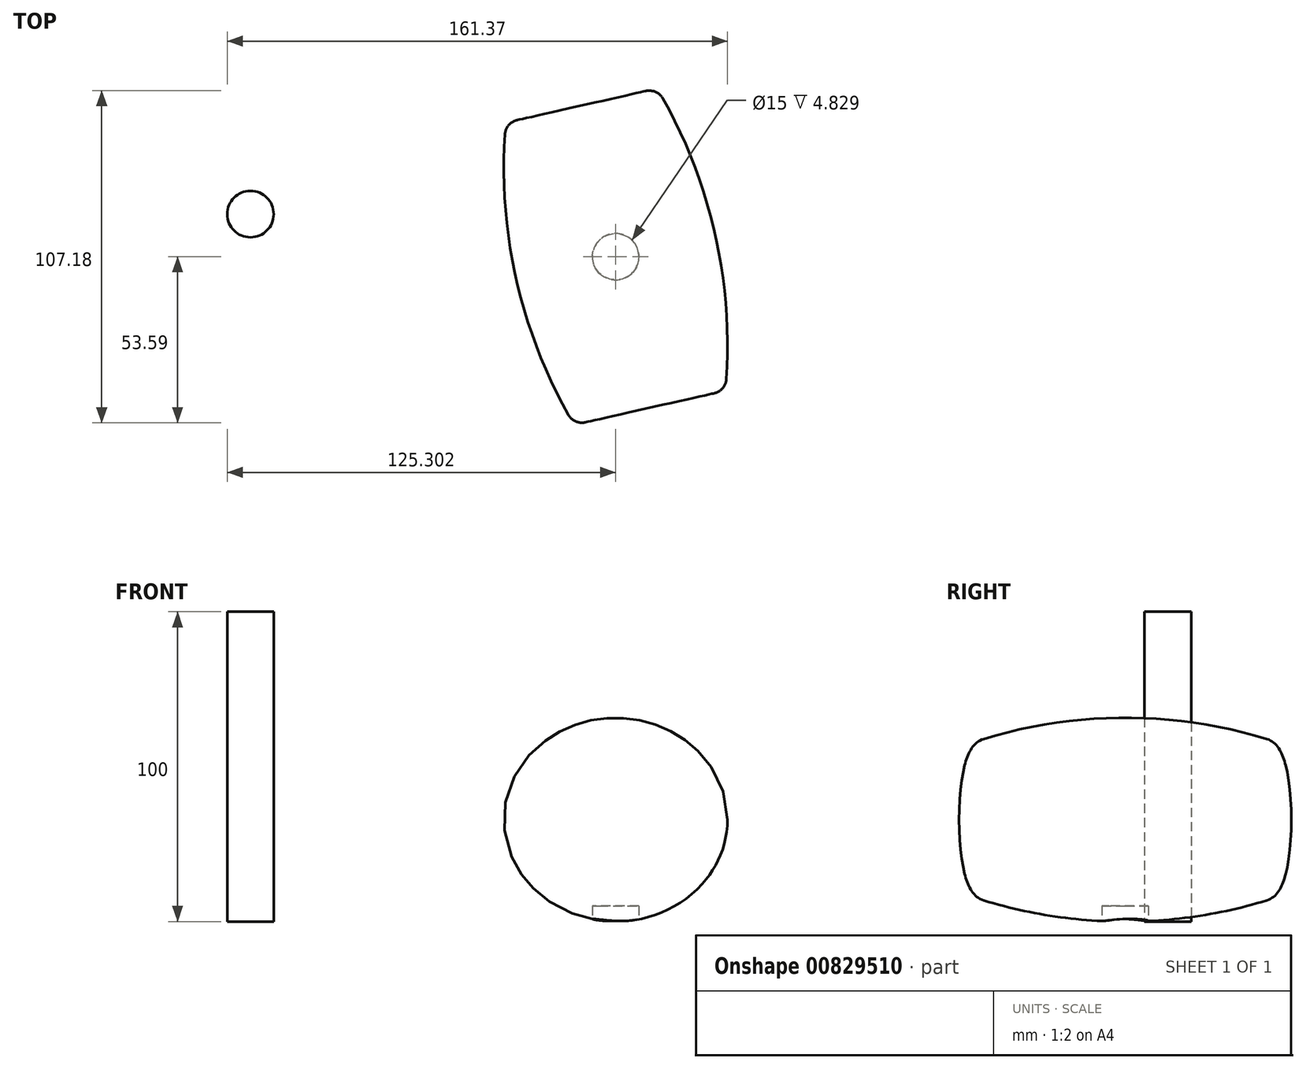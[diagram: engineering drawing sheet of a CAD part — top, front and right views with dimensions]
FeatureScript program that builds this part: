
annotation { "Feature Type Name" : "Feature", "Feature Type Description" : "" }
export const myFeature = defineFeature(function(context is Context, id is Id, definition is map)
    precondition{}
    {
        {
            var Q0;
            Q0=qCreatedBy(makeId("Top.planeOp"),FACE);
            var sketch = newSketch(context, id + "F0", { "sketchPlane" : qUnion([Q0])});
            skCircle(sketch, "E0", {"center": v(-56.5, 2) * mm, "radius": 7.5 * mm});
            skSolve(sketch);
        }
        {
            var Q0;
            Q0=makeQuery(id+"F0.imprint","IMPRINT",FACE,{"disambiguationData":[TD([[makeQuery(id+"F0.imprint","IMPRINT",EDGE,{"derivedFrom":sQuery(id+"F0.wireOp",EDGE,"E0")}),1.0]])]});
            extrude(context, id + "F1", {"entities" : qUnion([Q0]), "depth" : 100 * mm, "offsetDistance" : 25 * mm});
        }
        {
            var Q0;
            Q0=qCreatedBy(makeId("Top.planeOp"),FACE);
            var sketch = newSketch(context, id + "F2", { "sketchPlane" : qUnion([Q0])});
            skCircle(sketch, "E1", {"center": v(61.3, -11.75) * mm, "radius": 7.5 * mm});
            skLineSegment(sketch, "E2", {"start": v(61.3, -11.75) * mm, "end": v(68.6, -10.1) * mm, "construction": true});
            skSolve(sketch);
        }
        {
            var Q0;
            Q0=sQuery(id+"F2.wireOp",VERTEX,"E2.start");
            var Q1;
            Q1=sQuery(id+"F2.wireOp",EDGE,"E2");
            cPlane(context, id + "F3", {"entities" : qUnion([Q0, Q1]), "cplaneType" : CPlaneType.LINE_POINT, "offset" : 25 * mm, "width" : 150 * mm, "height" : 150 * mm});
        }
        {
            var Q0;
            Q0=qCreatedBy(id+"F3.planeOp",FACE);
            var sketch = newSketch(context, id + "F4", { "sketchPlane" : qUnion([Q0])});
            skArc(sketch, "E3", {"start": v(-74.96, 7.87) * mm, "mid": v(-24.96, 0) * mm, "end": v(25.04, 7.87) * mm});
            skPoint(sketch, "E4", {"position": v(-24.96, 0) * mm});
            skLineSegment(sketch, "E5", {"start": v(25.04, 7.87) * mm, "end": v(25.04, 32.87) * mm});
            skLineSegment(sketch, "E6", {"start": v(25.04, 32.87) * mm, "end": v(-74.96, 32.87) * mm});
            skLineSegment(sketch, "E7", {"start": v(-74.96, 32.87) * mm, "end": v(-74.96, 7.87) * mm});
            skSolve(sketch);
        }
        {
            var Q0;
            Q0=makeQuery(id+"F4.imprint","IMPRINT",FACE,{"disambiguationData":[TD([[makeQuery(id+"F4.imprint","IMPRINT",EDGE,{"derivedFrom":sQuery(id+"F4.wireOp",EDGE,"E3")}),1.0]])]});
            var Q1;
            Q1=sQuery(id+"F4.wireOp",EDGE,"E6");
            revolve(context, id + "F5", {"surfaceOperationType" : NewSurfaceOperationType.NEW, "entities" : qUnion([Q0]), "axis" : qUnion([Q1]), "revolveType" : RevolveType.FULL});
        }
        {
            var Q0;
            Q0=makeQuery(id+"F2.imprint","IMPRINT",FACE,{"disambiguationData":[TD([[makeQuery(id+"F2.imprint","IMPRINT",EDGE,{"derivedFrom":sQuery(id+"F2.wireOp",EDGE,"E1")}),1.0]])]});
            extrude(context, id + "F6", {"entities" : qUnion([Q0]), "operationType" : NewBodyOperationType.REMOVE, "depth" : 5 * mm, "offsetDistance" : 25 * mm});
        }
        {
            var Q0;
            Q0=makeQuery(id+"F5.opRevolve","SWEPT_FACE",FACE,{"disambiguationData":[OSD([sQuery(id+"F4.wireOp",EDGE,"E7")])]});
            var Q1;
            Q1=makeQuery(id+"F5.opRevolve","SWEPT_FACE",FACE,{"disambiguationData":[OSD([sQuery(id+"F4.wireOp",EDGE,"E5")])]});
            fillet(context, id + "F7", {"entities" : qUnion([Q0, Q1]), "radius" : 5 * mm, "tangentPropagation" : true, "allowEdgeOverflow" : false});
        }
    });
